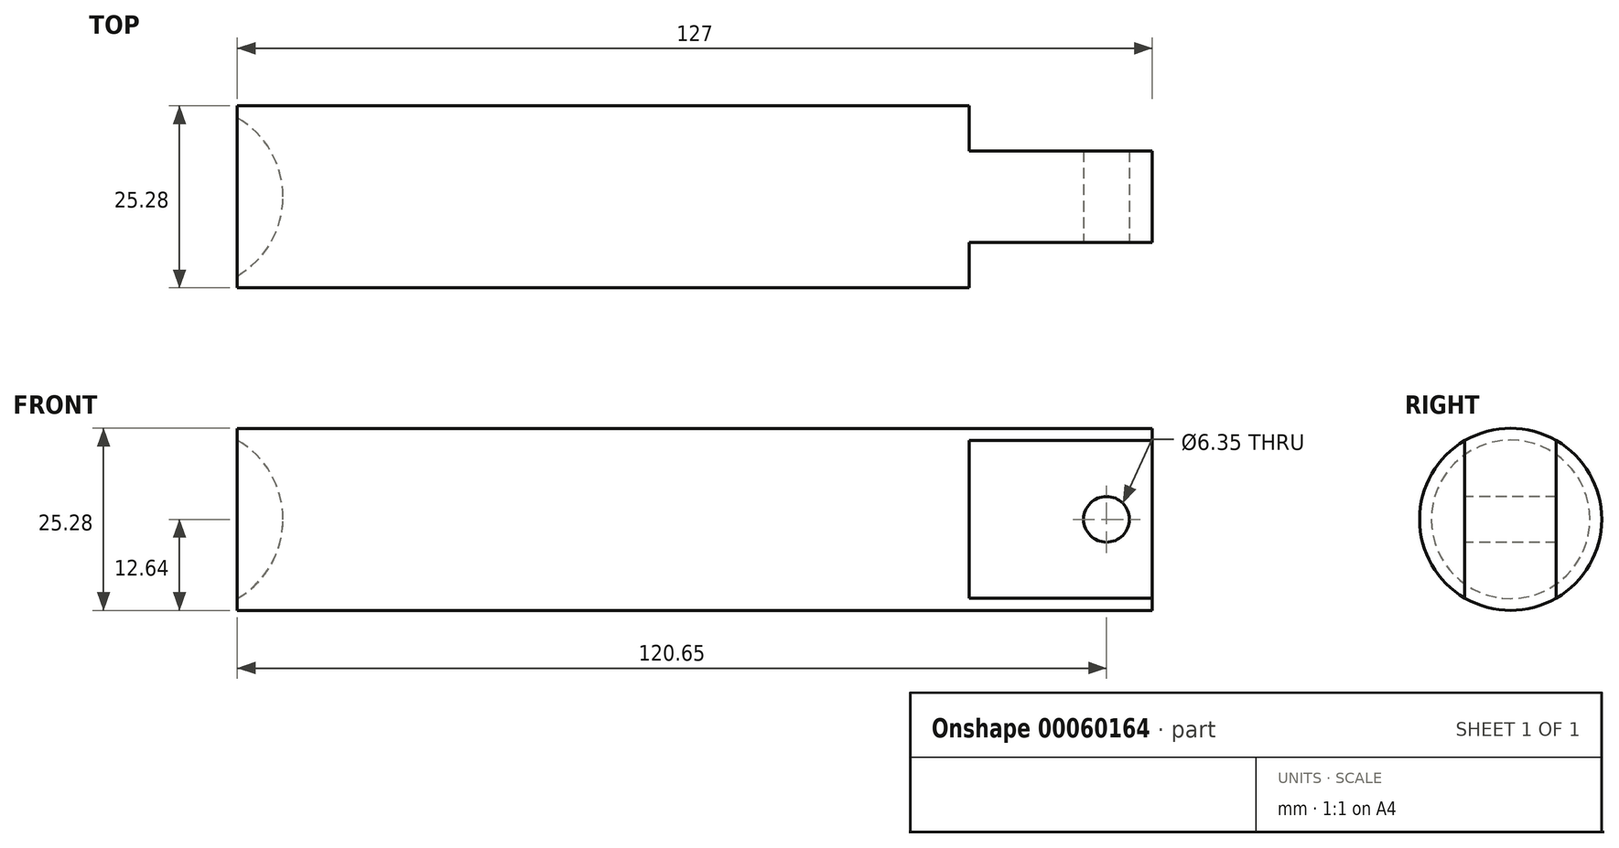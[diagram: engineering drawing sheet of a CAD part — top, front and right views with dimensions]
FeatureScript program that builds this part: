
annotation { "Feature Type Name" : "Feature", "Feature Type Description" : "" }
export const myFeature = defineFeature(function(context is Context, id is Id, definition is map)
    precondition{}
    {
        {
            var Q0;
            Q0=qCreatedBy(makeId("Right.planeOp"),FACE);
            var sketch = newSketch(context, id + "F0", { "sketchPlane" : qUnion([Q0])});
            skCircle(sketch, "E0", {"center": v(0, 0) * mm, "radius": 12.64 * mm});
            skSolve(sketch);
        }
        {
            var Q0;
            Q0 = qSketchRegion(id + "F0", true);
            extrude(context, id + "F1", {"entities" : qUnion([Q0]), "depth" : 101.6 * mm});
        }
        {
            var Q0;
            Q0=makeQuery(id+"F1.opExtrude","CAP_FACE",FACE,{"disambiguationData":[OSD([sQuery(id+"F0.wireOp",EDGE,"E0")])],"isStart":false});
            var sketch = newSketch(context, id + "F2", { "sketchPlane" : qUnion([Q0])});
            skLineSegment(sketch, "E1", {"start": v(-6.35, 10.93) * mm, "end": v(-6.35, -10.93) * mm});
            skLineSegment(sketch, "E2", {"start": v(6.35, 10.93) * mm, "end": v(6.35, -10.93) * mm});
            skArc(sketch, "E3", {"start": v(6.35, 10.93) * mm, "mid": v(0, 12.64) * mm, "end": v(-6.35, 10.93) * mm});
            skArc(sketch, "E4", {"start": v(-6.35, -10.93) * mm, "mid": v(0, -12.64) * mm, "end": v(6.35, -10.93) * mm});
            skSolve(sketch);
        }
        {
            var Q0;
            Q0 = qSketchRegion(id + "F2", true);
            extrude(context, id + "F3", {"entities" : qUnion([Q0]), "operationType" : NewBodyOperationType.ADD, "depth" : 25.4 * mm});
        }
        {
            var Q0;
            Q0=makeQuery(id+"F3.opExtrude","SWEPT_FACE",FACE,{"disambiguationData":[OSD([sQuery(id+"F2.wireOp",EDGE,"E1")])]});
            var sketch = newSketch(context, id + "F4", { "sketchPlane" : qUnion([Q0])});
            skCircle(sketch, "E5", {"center": v(120.65, 0) * mm, "radius": 3.18 * mm});
            skSolve(sketch);
        }
        {
            var Q0;
            Q0=makeQuery(id+"F4.imprint","IMPRINT",FACE,{"disambiguationData":[TD([[makeQuery(id+"F4.imprint","IMPRINT",EDGE,{"derivedFrom":sQuery(id+"F4.wireOp",EDGE,"E5")}),1.0]])]});
            var Q1;
            Q1=makeQuery(id+"F3.opExtrude","SWEPT_FACE",FACE,{"disambiguationData":[OSD([sQuery(id+"F2.wireOp",EDGE,"E2")])]});
            extrude(context, id + "F5", {"entities" : qUnion([Q0]), "operationType" : NewBodyOperationType.REMOVE, "endBound" : BoundingType.UP_TO_SURFACE, "oppositeDirection" : true, "endBoundEntityFace" : qUnion([Q1]), "depth" : 25.4 * mm});
        }
        {
            var Q0;
            Q0=qCreatedBy(makeId("Front.planeOp"),FACE);
            var sketch = newSketch(context, id + "F6", { "sketchPlane" : qUnion([Q0])});
            skArc(sketch, "E6", {"start": v(0, 11) * mm, "mid": v(4.65, 6.35) * mm, "end": v(6.35, 0) * mm});
            skLineSegment(sketch, "E7", {"start": v(6.35, 0) * mm, "end": v(0, 0) * mm});
            skLineSegment(sketch, "E8", {"start": v(0, 0) * mm, "end": v(0, 11) * mm});
            skSolve(sketch);
        }
        {
            var Q0;
            Q0 = qSketchRegion(id + "F6", true);
            var Q1;
            Q1=sQuery(id+"F6.wireOp",EDGE,"E7");
            revolve(context, id + "F7", {"operationType" : NewBodyOperationType.REMOVE, "entities" : qUnion([Q0]), "axis" : qUnion([Q1]), "revolveType" : RevolveType.FULL});
        }
    });
